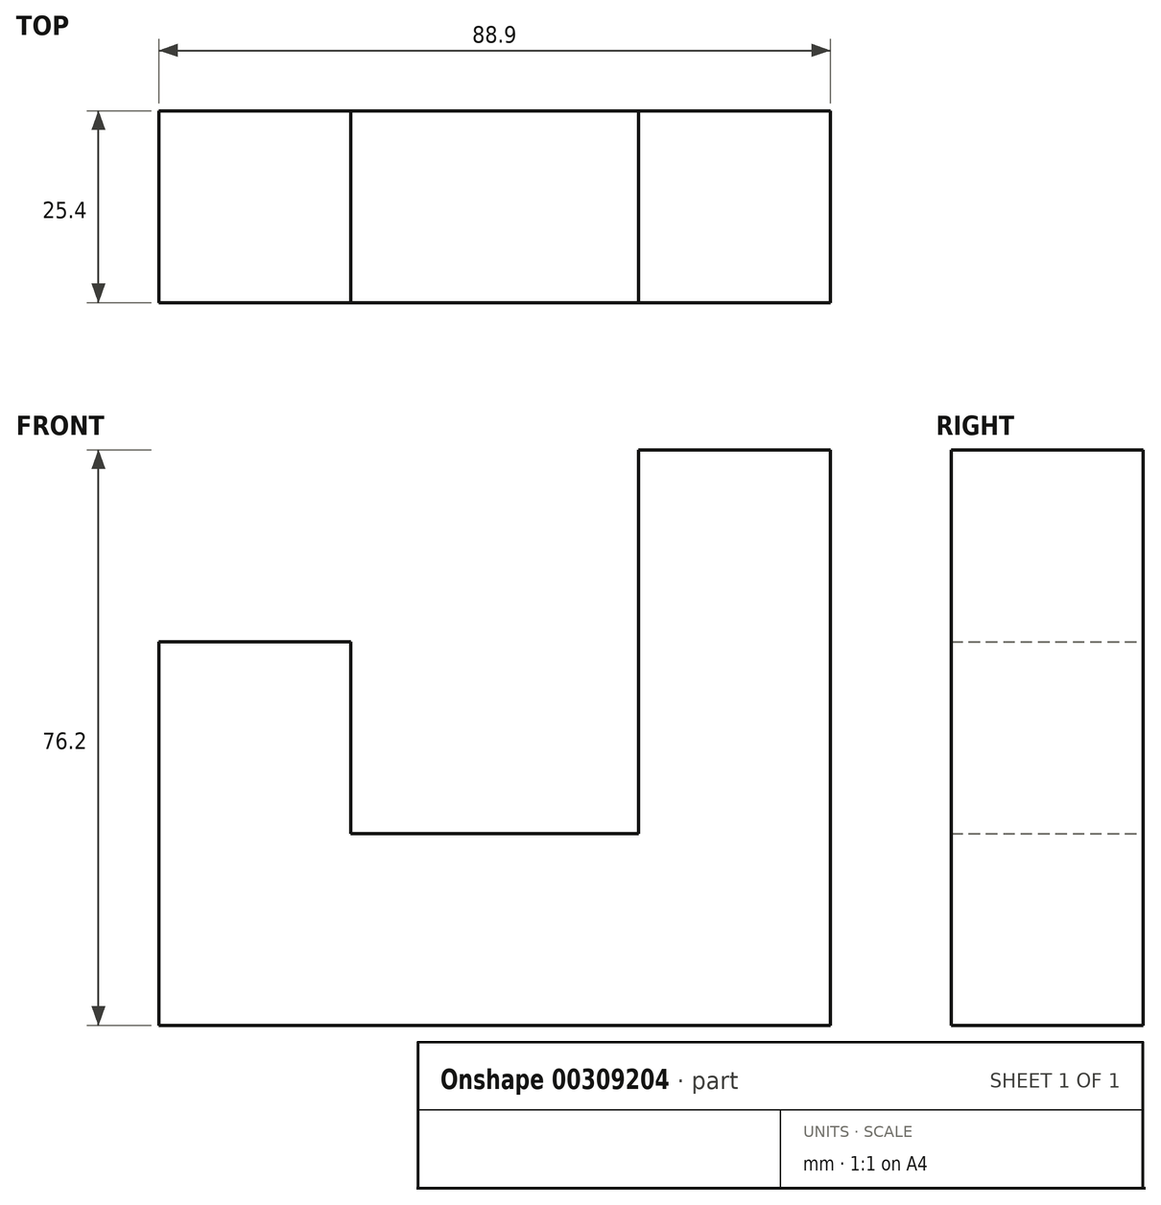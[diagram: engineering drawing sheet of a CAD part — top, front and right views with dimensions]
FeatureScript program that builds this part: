
annotation { "Feature Type Name" : "Feature", "Feature Type Description" : "" }
export const myFeature = defineFeature(function(context is Context, id is Id, definition is map)
    precondition{}
    {
        {
            var Q0;
            Q0=qCreatedBy(makeId("Front.planeOp"),FACE);
            var sketch = newSketch(context, id + "F0", { "sketchPlane" : qUnion([Q0])});
            skLineSegment(sketch, "E0", {"start": v(-43.28, -2.52) * mm, "end": v(-17.88, -2.52) * mm});
            skLineSegment(sketch, "E1", {"start": v(-17.88, -2.52) * mm, "end": v(-17.88, -27.92) * mm});
            skLineSegment(sketch, "E2", {"start": v(-17.88, -27.92) * mm, "end": v(20.22, -27.92) * mm});
            skLineSegment(sketch, "E3", {"start": v(20.22, -27.92) * mm, "end": v(20.22, 22.88) * mm});
            skLineSegment(sketch, "E4", {"start": v(20.22, 22.88) * mm, "end": v(45.62, 22.88) * mm});
            skLineSegment(sketch, "E5", {"start": v(45.62, 22.88) * mm, "end": v(45.62, -53.32) * mm});
            skLineSegment(sketch, "E6", {"start": v(45.62, -53.32) * mm, "end": v(-43.28, -53.32) * mm});
            skLineSegment(sketch, "E7", {"start": v(-43.28, -53.32) * mm, "end": v(-43.28, -2.52) * mm});
            skSolve(sketch);
        }
        {
            var Q0;
            Q0=makeQuery(id+"F0.imprint","IMPRINT",FACE,{"disambiguationData":[TD([[makeQuery(id+"F0.imprint","IMPRINT",EDGE,{"derivedFrom":sQuery(id+"F0.wireOp",EDGE,"E0")}),-1.0]])]});
            extrude(context, id + "F1", {"entities" : qUnion([Q0]), "depth" : 25.4 * mm});
        }
    });
